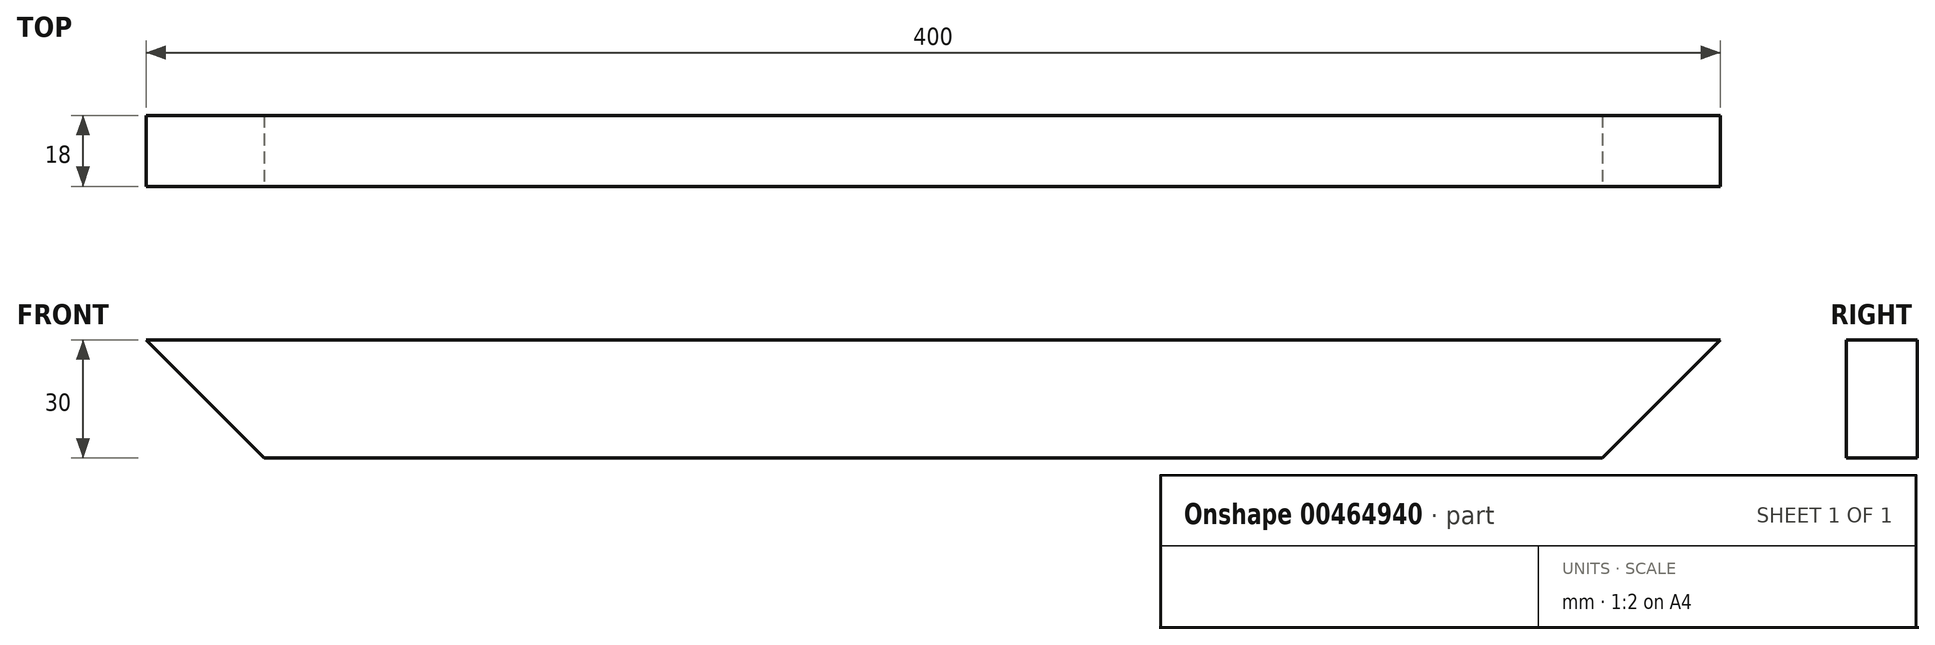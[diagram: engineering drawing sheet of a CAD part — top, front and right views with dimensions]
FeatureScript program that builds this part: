
annotation { "Feature Type Name" : "Feature", "Feature Type Description" : "" }
export const myFeature = defineFeature(function(context is Context, id is Id, definition is map)
    precondition{}
    {
        {
            var Q0;
            Q0=qCreatedBy(makeId("Right.planeOp"),FACE);
            var sketch = newSketch(context, id + "F0", { "sketchPlane" : qUnion([Q0])});
            skLineSegment(sketch, "E0.bottom", {"start": v(-9, 15) * mm, "end": v(9, 15) * mm});
            skLineSegment(sketch, "E0.top", {"start": v(-9, -15) * mm, "end": v(9, -15) * mm});
            skLineSegment(sketch, "E0.left", {"start": v(-9, 15) * mm, "end": v(-9, -15) * mm});
            skLineSegment(sketch, "E0.right", {"start": v(9, 15) * mm, "end": v(9, -15) * mm});
            skPoint(sketch, "E0.middle", {"position": v(0, 0) * mm});
            skSolve(sketch);
        }
        {
            var Q0;
            Q0=makeQuery(id+"F0.imprint","IMPRINT",FACE,{"disambiguationData":[TD([[makeQuery(id+"F0.imprint","IMPRINT",EDGE,{"derivedFrom":sQuery(id+"F0.wireOp",EDGE,"E0.bottom")}),-1.0]])]});
            extrude(context, id + "F1", {"entities" : qUnion([Q0]), "endBound" : BoundingType.SYMMETRIC, "depth" : 400 * mm, "offsetDistance" : 25 * mm});
        }
        {
            var Q0;
            Q0=makeQuery(id+"F1.opExtrude","SWEPT_FACE",FACE,{"disambiguationData":[OSD([sQuery(id+"F0.wireOp",EDGE,"E0.left")])]});
            var sketch = newSketch(context, id + "F2", { "sketchPlane" : qUnion([Q0])});
            skLineSegment(sketch, "E1", {"start": v(-200, 15) * mm, "end": v(-170, -15) * mm});
            skLineSegment(sketch, "E2", {"start": v(-170, -15) * mm, "end": v(-200, -15) * mm});
            skLineSegment(sketch, "E3", {"start": v(-200, -15) * mm, "end": v(-200, 15) * mm});
            skLineSegment(sketch, "E4", {"start": v(0, 15) * mm, "end": v(0, -15) * mm, "construction": true});
            skLineSegment(sketch, "E5.MirrorCS", {"start": v(200, 15) * mm, "end": v(170, -15) * mm});
            skLineSegment(sketch, "E6.MirrorCS", {"start": v(170, -15) * mm, "end": v(200, -15) * mm});
            skLineSegment(sketch, "E7.MirrorCS", {"start": v(200, -15) * mm, "end": v(200, 15) * mm});
            skSolve(sketch);
        }
        {
            var Q0;
            Q0=makeQuery(id+"F2.imprint","IMPRINT",FACE,{"disambiguationData":[TD([[makeQuery(id+"F2.imprint","IMPRINT",EDGE,{"derivedFrom":sQuery(id+"F2.wireOp",EDGE,"E1")}),-1.0]])]});
            var Q1;
            Q1=makeQuery(id+"F2.imprint","IMPRINT",FACE,{"disambiguationData":[TD([[makeQuery(id+"F2.imprint","IMPRINT",EDGE,{"derivedFrom":sQuery(id+"F2.wireOp",EDGE,"E5.MirrorCS")}),1.0]])]});
            extrude(context, id + "F3", {"entities" : qUnion([Q0, Q1]), "operationType" : NewBodyOperationType.REMOVE, "oppositeDirection" : true, "depth" : 18 * mm, "offsetDistance" : 25 * mm});
        }
    });
